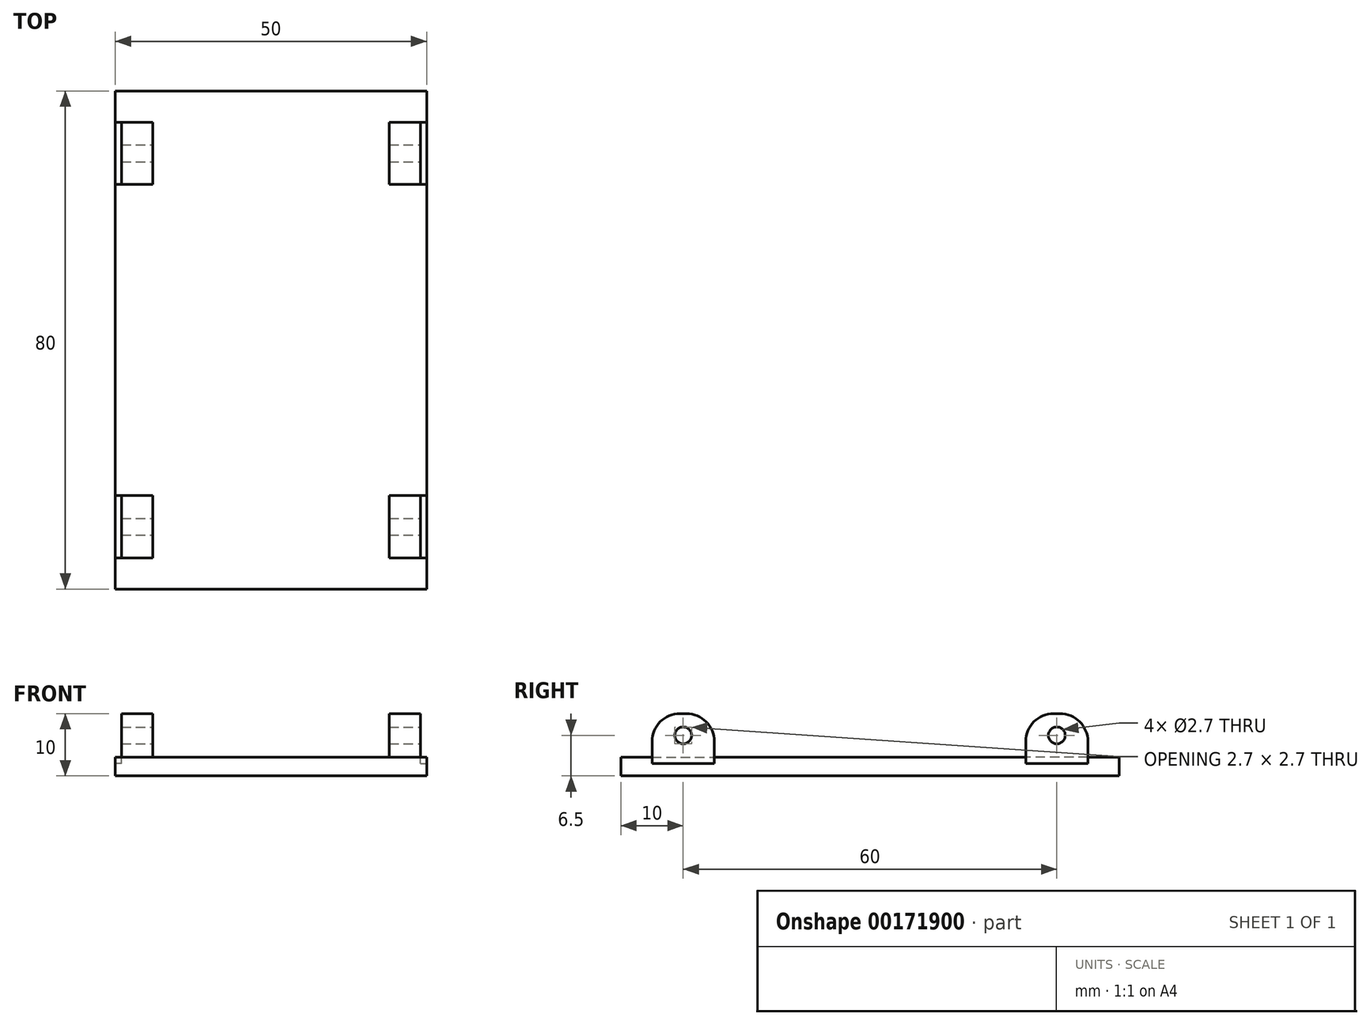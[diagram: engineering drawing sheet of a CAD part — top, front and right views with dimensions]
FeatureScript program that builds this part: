
annotation { "Feature Type Name" : "Feature", "Feature Type Description" : "" }
export const myFeature = defineFeature(function(context is Context, id is Id, definition is map)
    precondition{}
    {
        {
            var Q0;
            Q0=qCreatedBy(makeId("Top.planeOp"),FACE);
            var sketch = newSketch(context, id + "F0", { "sketchPlane" : qUnion([Q0])});
            skLineSegment(sketch, "E0.bottom", {"start": v(-25, 40) * mm, "end": v(25, 40) * mm});
            skLineSegment(sketch, "E0.top", {"start": v(-25, -40) * mm, "end": v(25, -40) * mm});
            skLineSegment(sketch, "E0.left", {"start": v(-25, 40) * mm, "end": v(-25, -40) * mm});
            skLineSegment(sketch, "E0.right", {"start": v(25, 40) * mm, "end": v(25, -40) * mm});
            skPoint(sketch, "E0.middle", {"position": v(0, 0) * mm});
            skSolve(sketch);
        }
        {
            var Q0;
            Q0 = qSketchRegion(id + "F0", true);
            extrude(context, id + "F1", {"entities" : qUnion([Q0]), "depth" : 3 * mm});
        }
        {
            var Q0;
            Q0=makeQuery(id+"F1.opExtrude","CAP_FACE",FACE,{"disambiguationData":[OSD([sQuery(id+"F0.wireOp",EDGE,"E0.bottom"),sQuery(id+"F0.wireOp",EDGE,"E0.top"),sQuery(id+"F0.wireOp",EDGE,"E0.left"),sQuery(id+"F0.wireOp",EDGE,"E0.right")])],"isStart":false});
            var sketch = newSketch(context, id + "F2", { "sketchPlane" : qUnion([Q0])});
            skLineSegment(sketch, "E1.bottom", {"start": v(-25, 35) * mm, "end": v(-19, 35) * mm});
            skLineSegment(sketch, "E1.top", {"start": v(-25, 25) * mm, "end": v(-19, 25) * mm});
            skLineSegment(sketch, "E1.left", {"start": v(-25, 35) * mm, "end": v(-25, 25) * mm});
            skLineSegment(sketch, "E1.right", {"start": v(-19, 35) * mm, "end": v(-19, 25) * mm});
            skLineSegment(sketch, "E2.MirrorCS", {"start": v(19, 35) * mm, "end": v(19, 25) * mm});
            skLineSegment(sketch, "E3.MirrorCS", {"start": v(25, 25) * mm, "end": v(19, 25) * mm});
            skLineSegment(sketch, "E4.MirrorCS", {"start": v(25, 35) * mm, "end": v(19, 35) * mm});
            skLineSegment(sketch, "E5.MirrorCS", {"start": v(25, 35) * mm, "end": v(25, 25) * mm});
            skLineSegment(sketch, "E6.MirrorCS", {"start": v(-25, -25) * mm, "end": v(-19, -25) * mm});
            skLineSegment(sketch, "E7.MirrorCS", {"start": v(-25, -35) * mm, "end": v(-25, -25) * mm});
            skLineSegment(sketch, "E8.MirrorCS", {"start": v(-19, -35) * mm, "end": v(-19, -25) * mm});
            skLineSegment(sketch, "E9.MirrorCS", {"start": v(-25, -35) * mm, "end": v(-19, -35) * mm});
            skLineSegment(sketch, "E10.MirrorCS", {"start": v(19, -35) * mm, "end": v(19, -25) * mm});
            skLineSegment(sketch, "E11.MirrorCS", {"start": v(25, -35) * mm, "end": v(25, -25) * mm});
            skLineSegment(sketch, "E12.MirrorCS", {"start": v(25, -35) * mm, "end": v(19, -35) * mm});
            skLineSegment(sketch, "E13.MirrorCS", {"start": v(25, -25) * mm, "end": v(19, -25) * mm});
            skSolve(sketch);
        }
        {
            var Q0;
            Q0 = qSketchRegion(id + "F2", true);
            extrude(context, id + "F3", {"entities" : qUnion([Q0]), "operationType" : NewBodyOperationType.ADD, "depth" : 7 * mm});
        }
        {
            var Q0;
            Q0=makeQuery(id+"F3.boolean.opBoolean","MERGE",FACE,{"derivedFrom":[makeQuery(id+"F1.opExtrude","SWEPT_FACE",FACE,{"disambiguationData":[OSD([sQuery(id+"F0.wireOp",EDGE,"E0.right")])]}),makeQuery(id+"F3.opExtrude","SWEPT_FACE",FACE,{"disambiguationData":[OSD([sQuery(id+"F2.wireOp",EDGE,"E5.MirrorCS")])]}),makeQuery(id+"F3.opExtrude","SWEPT_FACE",FACE,{"disambiguationData":[OSD([sQuery(id+"F2.wireOp",EDGE,"E11.MirrorCS")])]})]});
            var sketch = newSketch(context, id + "F4", { "sketchPlane" : qUnion([Q0])});
            skCircle(sketch, "E14", {"center": v(-30, 6.5) * mm, "radius": 1.35 * mm});
            skPoint(sketch, "E14.centerSnap0", {"position": v(-35, 6.5) * mm});
            skPoint(sketch, "E14.centerSnap1", {"position": v(-30, 10) * mm});
            skCircle(sketch, "E15.MirrorC", {"center": v(30, 6.5) * mm, "radius": 1.35 * mm});
            skSolve(sketch);
        }
        {
            var Q0;
            Q0 = qSketchRegion(id + "F4", true);
            extrude(context, id + "F5", {"entities" : qUnion([Q0]), "operationType" : NewBodyOperationType.REMOVE, "endBound" : BoundingType.THROUGH_ALL, "oppositeDirection" : true, "depth" : 25 * mm});
        }
        {
            var Q0;
            Q0=makeQuery(id+"F3.opExtrude","CAP_EDGE",EDGE,{"disambiguationData":[OSD([sQuery(id+"F2.wireOp",EDGE,"E12.MirrorCS")])],"isStart":false});
            var Q1;
            Q1=makeQuery(id+"F3.opExtrude","CAP_EDGE",EDGE,{"disambiguationData":[OSD([sQuery(id+"F2.wireOp",EDGE,"E13.MirrorCS")])],"isStart":false});
            var Q2;
            Q2=makeQuery(id+"F3.opExtrude","CAP_EDGE",EDGE,{"disambiguationData":[OSD([sQuery(id+"F2.wireOp",EDGE,"E9.MirrorCS")])],"isStart":false});
            var Q3;
            Q3=makeQuery(id+"F3.opExtrude","CAP_EDGE",EDGE,{"disambiguationData":[OSD([sQuery(id+"F2.wireOp",EDGE,"E6.MirrorCS")])],"isStart":false});
            var Q4;
            Q4=makeQuery(id+"F3.opExtrude","CAP_EDGE",EDGE,{"disambiguationData":[OSD([sQuery(id+"F2.wireOp",EDGE,"E1.top")])],"isStart":false});
            var Q5;
            Q5=makeQuery(id+"F3.opExtrude","CAP_EDGE",EDGE,{"disambiguationData":[OSD([sQuery(id+"F2.wireOp",EDGE,"E1.bottom")])],"isStart":false});
            var Q6;
            Q6=makeQuery(id+"F3.opExtrude","CAP_EDGE",EDGE,{"disambiguationData":[OSD([sQuery(id+"F2.wireOp",EDGE,"E3.MirrorCS")])],"isStart":false});
            var Q7;
            Q7=makeQuery(id+"F3.opExtrude","CAP_EDGE",EDGE,{"disambiguationData":[OSD([sQuery(id+"F2.wireOp",EDGE,"E4.MirrorCS")])],"isStart":false});
            fillet(context, id + "F6", {"entities" : qUnion([Q0, Q1, Q2, Q3, Q4, Q5, Q6, Q7]), "radius" : 4.5 * mm, "tangentPropagation" : true, "allowEdgeOverflow" : false});
        }
        {
            var Q0;
            Q0=makeQuery(id+"F3.boolean.opBoolean","MERGE",FACE,{"derivedFrom":[makeQuery(id+"F1.opExtrude","SWEPT_FACE",FACE,{"disambiguationData":[OSD([sQuery(id+"F0.wireOp",EDGE,"E0.right")])]}),makeQuery(id+"F3.opExtrude","SWEPT_FACE",FACE,{"disambiguationData":[OSD([sQuery(id+"F2.wireOp",EDGE,"E5.MirrorCS")])]}),makeQuery(id+"F3.opExtrude","SWEPT_FACE",FACE,{"disambiguationData":[OSD([sQuery(id+"F2.wireOp",EDGE,"E11.MirrorCS")])]})]});
            var sketch = newSketch(context, id + "F7", { "sketchPlane" : qUnion([Q0])});
            skLineSegment(sketch, "E16", {"start": v(-35, 3) * mm, "end": v(-25, 3) * mm});
            skLineSegment(sketch, "E17", {"start": v(25, 3) * mm, "end": v(35, 3) * mm});
            skSolve(sketch);
        }
        {
            var Q0;
            Q0 = qSketchRegion(id + "F7", true);
            var Q1;
            Q1=makeQuery(id+"F7.imprint","IMPRINT",FACE,{"disambiguationData":[TD([[makeQuery(id+"F7.imprint","IMPRINT",EDGE,{"derivedFrom":sQuery(id+"F7.wireOp",EDGE,"E16")}),1.0]])]});
            var Q2;
            Q2=makeQuery(id+"F7.imprint","IMPRINT",FACE,{"disambiguationData":[TD([[makeQuery(id+"F7.imprint","IMPRINT",EDGE,{"derivedFrom":sQuery(id+"F7.wireOp",EDGE,"E17")}),1.0]])]});
            extrude(context, id + "F8", {"entities" : qUnion([Q0, Q1, Q2]), "operationType" : NewBodyOperationType.REMOVE, "oppositeDirection" : true, "depth" : 1 * mm});
        }
        {
            var Q0;
            Q0=makeQuery(id+"F3.boolean.opBoolean","MERGE",FACE,{"derivedFrom":[makeQuery(id+"F1.opExtrude","SWEPT_FACE",FACE,{"disambiguationData":[OSD([sQuery(id+"F0.wireOp",EDGE,"E0.left")])]}),makeQuery(id+"F3.opExtrude","SWEPT_FACE",FACE,{"disambiguationData":[OSD([sQuery(id+"F2.wireOp",EDGE,"E1.left")])]}),makeQuery(id+"F3.opExtrude","SWEPT_FACE",FACE,{"disambiguationData":[OSD([sQuery(id+"F2.wireOp",EDGE,"E7.MirrorCS")])]})]});
            var sketch = newSketch(context, id + "F9", { "sketchPlane" : qUnion([Q0])});
            skLineSegment(sketch, "E18", {"start": v(-35, 3) * mm, "end": v(-25, 3) * mm});
            skLineSegment(sketch, "E19", {"start": v(25, 3) * mm, "end": v(35, 3) * mm});
            skSolve(sketch);
        }
        {
            var Q0;
            Q0 = qSketchRegion(id + "F9", true);
            var Q1;
            Q1=makeQuery(id+"F9.imprint","IMPRINT",FACE,{"disambiguationData":[TD([[makeQuery(id+"F9.imprint","IMPRINT",EDGE,{"derivedFrom":sQuery(id+"F9.wireOp",EDGE,"E18")}),1.0]])]});
            var Q2;
            Q2=makeQuery(id+"F9.imprint","IMPRINT",FACE,{"disambiguationData":[TD([[makeQuery(id+"F9.imprint","IMPRINT",EDGE,{"derivedFrom":sQuery(id+"F9.wireOp",EDGE,"E19")}),1.0]])]});
            extrude(context, id + "F10", {"entities" : qUnion([Q0, Q1, Q2]), "operationType" : NewBodyOperationType.REMOVE, "oppositeDirection" : true, "depth" : 1 * mm});
        }
        {
            var Q0;
            Q0=makeQuery(id+"F10.boolean.opBoolean","MERGE",FACE,{"derivedFrom":[makeQuery(id+"F8.boolean.opBoolean","MERGE",FACE,{"derivedFrom":[makeQuery(id+"F1.opExtrude","CAP_FACE",FACE,{"disambiguationData":[OSD([sQuery(id+"F0.wireOp",EDGE,"E0.bottom"),sQuery(id+"F0.wireOp",EDGE,"E0.top"),sQuery(id+"F0.wireOp",EDGE,"E0.left"),sQuery(id+"F0.wireOp",EDGE,"E0.right")])],"isStart":false}),makeQuery(id+"F8.opExtrude","SWEPT_FACE",FACE,{"disambiguationData":[OSD([sQuery(id+"F7.wireOp",EDGE,"E16")])]}),makeQuery(id+"F8.opExtrude","SWEPT_FACE",FACE,{"disambiguationData":[OSD([sQuery(id+"F7.wireOp",EDGE,"E17")])]})]}),makeQuery(id+"F10.opExtrude","SWEPT_FACE",FACE,{"disambiguationData":[OSD([sQuery(id+"F9.wireOp",EDGE,"E18")])]}),makeQuery(id+"F10.opExtrude","SWEPT_FACE",FACE,{"disambiguationData":[OSD([sQuery(id+"F9.wireOp",EDGE,"E19")])]})]});
            var sketch = newSketch(context, id + "F11", { "sketchPlane" : qUnion([Q0])});
            skLineSegment(sketch, "E20.bottom", {"start": v(-24, 35) * mm, "end": v(-25, 35) * mm});
            skLineSegment(sketch, "E20.top", {"start": v(-24, 25) * mm, "end": v(-25, 25) * mm});
            skLineSegment(sketch, "E20.left", {"start": v(-24, 35) * mm, "end": v(-24, 25) * mm});
            skLineSegment(sketch, "E20.right", {"start": v(-25, 35) * mm, "end": v(-25, 25) * mm});
            skLineSegment(sketch, "E21.MirrorCS", {"start": v(-24, -25) * mm, "end": v(-25, -25) * mm});
            skLineSegment(sketch, "E22.MirrorCS", {"start": v(-24, -35) * mm, "end": v(-25, -35) * mm});
            skLineSegment(sketch, "E23.MirrorCS", {"start": v(24, 25) * mm, "end": v(25, 25) * mm});
            skLineSegment(sketch, "E24.MirrorCS", {"start": v(24, 35) * mm, "end": v(25, 35) * mm});
            skLineSegment(sketch, "E25.MirrorCS", {"start": v(24, -25) * mm, "end": v(25, -25) * mm});
            skLineSegment(sketch, "E26.MirrorCS", {"start": v(24, -35) * mm, "end": v(25, -35) * mm});
            skSolve(sketch);
        }
        {
            var Q0;
            Q0 = qSketchRegion(id + "F11", true);
            var Q1;
            {var subQ0=sQuery(id+"F11.wireOp",EDGE,"E23.MirrorCS");Q1=makeQuery(id+"F11.imprint","IMPRINT",FACE,{"disambiguationData":[TD([[makeQuery(id+"F11.imprint","IMPRINT",EDGE,{"derivedFrom":subQ0}),1.0]])]});}
            var Q2;
            {var subQ0=sQuery(id+"F11.wireOp",EDGE,"E25.MirrorCS");Q2=makeQuery(id+"F11.imprint","IMPRINT",FACE,{"disambiguationData":[TD([[makeQuery(id+"F11.imprint","IMPRINT",EDGE,{"derivedFrom":subQ0}),-1.0]])]});}
            var Q3;
            {var subQ0=sQuery(id+"F11.wireOp",EDGE,"E21.MirrorCS");Q3=makeQuery(id+"F11.imprint","IMPRINT",FACE,{"disambiguationData":[TD([[makeQuery(id+"F11.imprint","IMPRINT",EDGE,{"derivedFrom":subQ0}),1.0]])]});}
            extrude(context, id + "F12", {"entities" : qUnion([Q0, Q1, Q2, Q3]), "operationType" : NewBodyOperationType.REMOVE, "oppositeDirection" : true, "depth" : 1 * mm});
        }
    });
